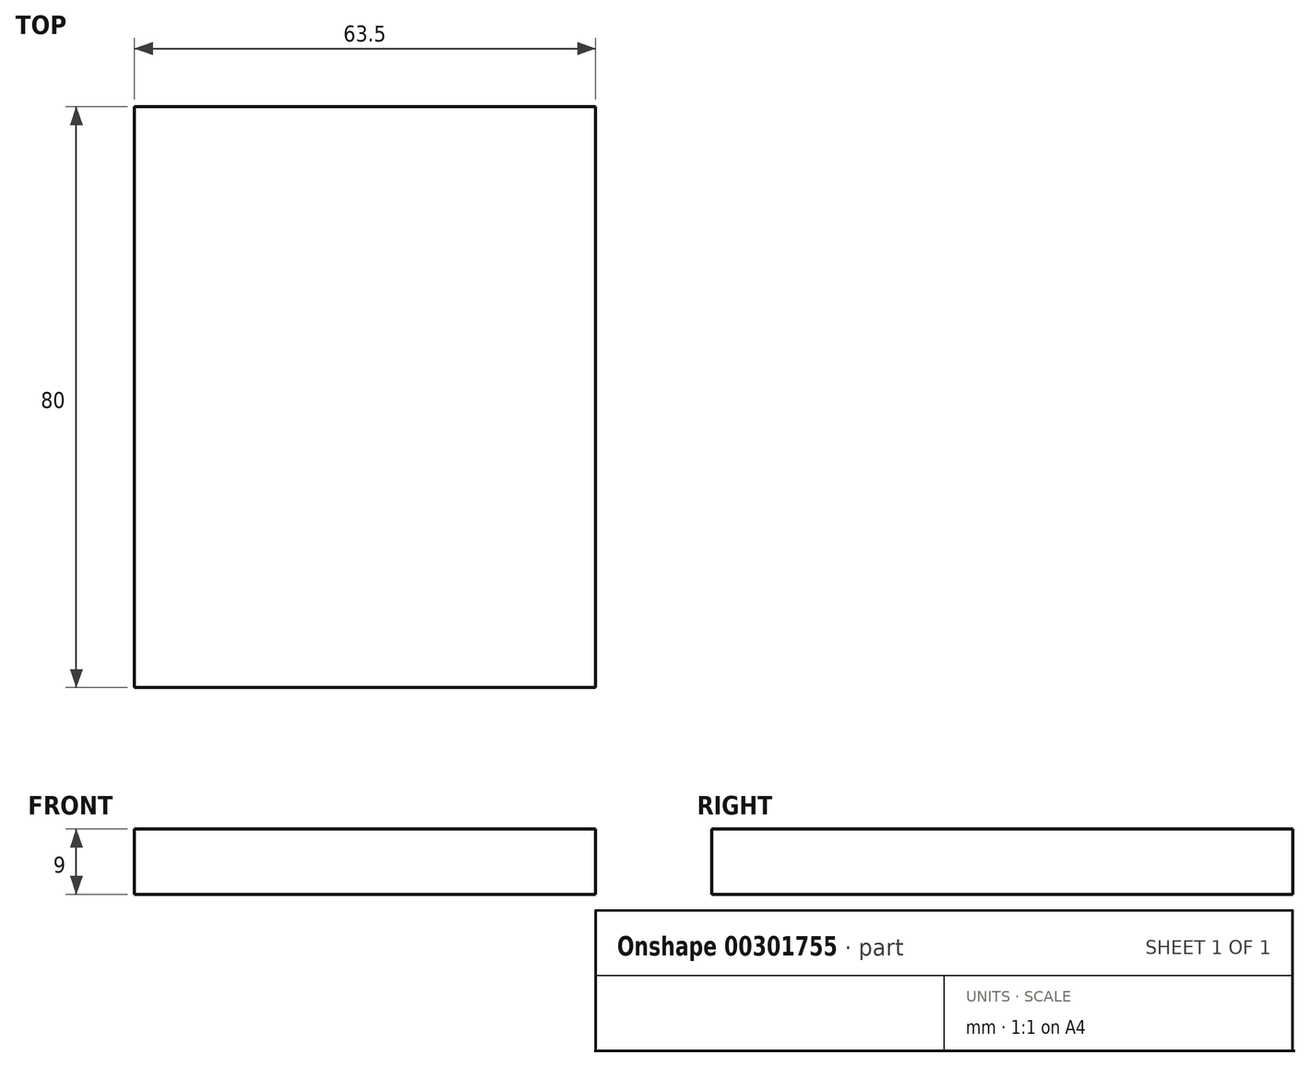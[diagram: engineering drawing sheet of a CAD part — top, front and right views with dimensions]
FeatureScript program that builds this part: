
annotation { "Feature Type Name" : "Feature", "Feature Type Description" : "" }
export const myFeature = defineFeature(function(context is Context, id is Id, definition is map)
    precondition{}
    {
        {
            var Q0;
            Q0=qCreatedBy(makeId("Top.planeOp"),FACE);
            var sketch = newSketch(context, id + "F0", { "sketchPlane" : qUnion([Q0])});
            skLineSegment(sketch, "E0.bottom", {"start": v(-63.5, 71.26) * mm, "end": v(0, 71.26) * mm});
            skLineSegment(sketch, "E0.top", {"start": v(-63.5, -8.74) * mm, "end": v(0, -8.74) * mm});
            skLineSegment(sketch, "E0.left", {"start": v(-63.5, 71.26) * mm, "end": v(-63.5, -8.74) * mm});
            skLineSegment(sketch, "E0.right", {"start": v(0, 71.26) * mm, "end": v(0, -8.74) * mm});
            skSolve(sketch);
        }
        {
            var Q0;
            Q0=makeQuery(id+"F0.imprint","IMPRINT",FACE,{"disambiguationData":[TD([[makeQuery(id+"F0.imprint","IMPRINT",EDGE,{"derivedFrom":sQuery(id+"F0.wireOp",EDGE,"E0.bottom")}),-1.0]])]});
            extrude(context, id + "F1", {"entities" : qUnion([Q0]), "oppositeDirection" : true, "depth" : 9 * mm});
        }
    });
